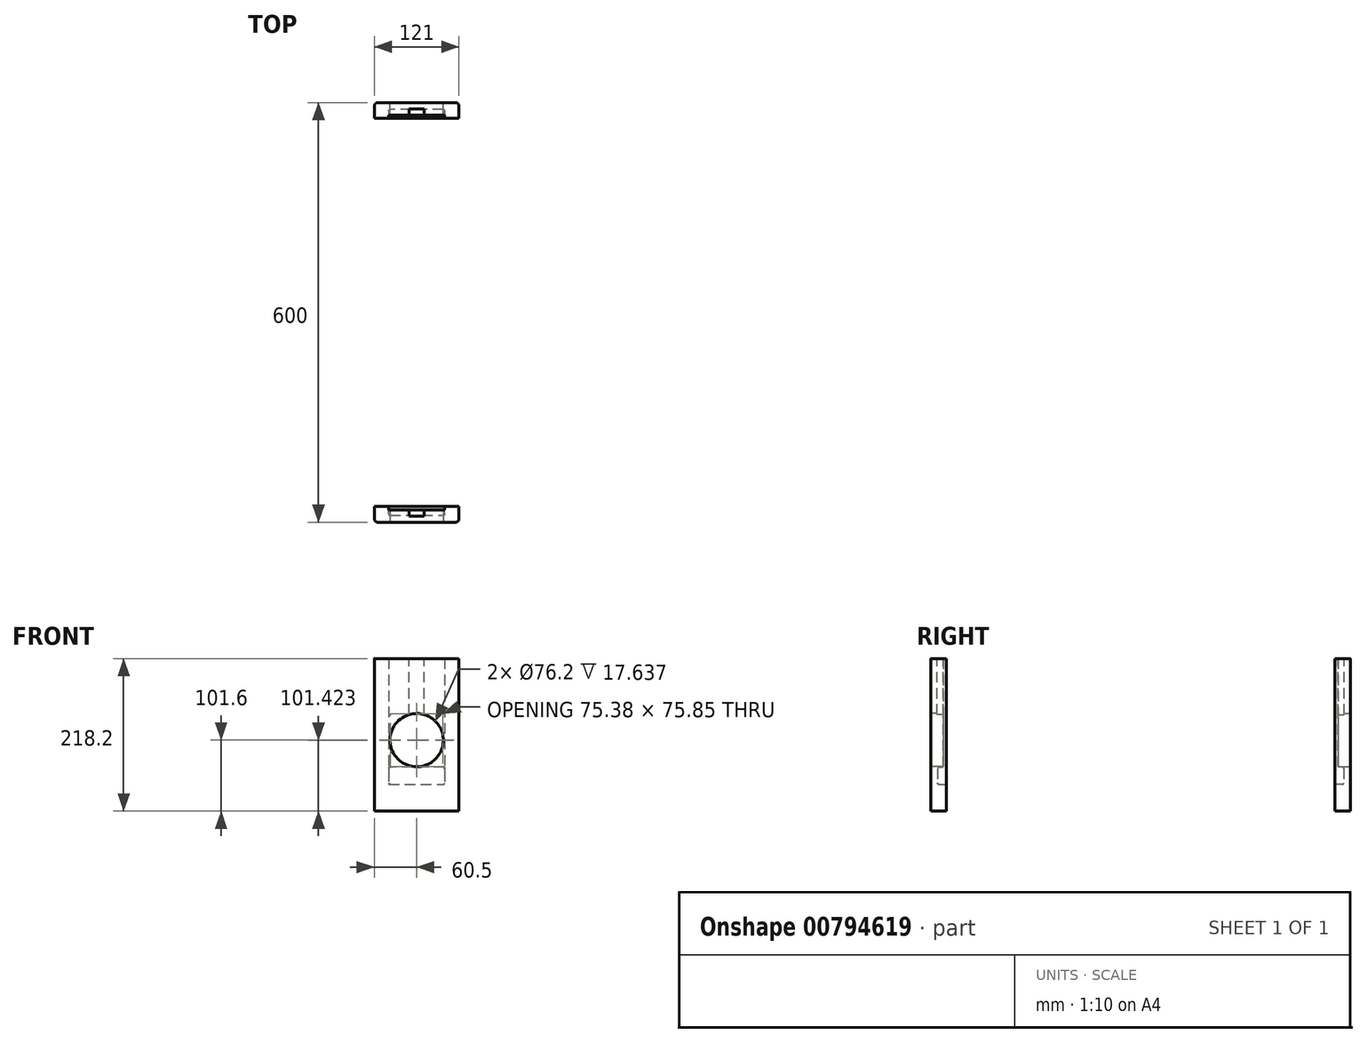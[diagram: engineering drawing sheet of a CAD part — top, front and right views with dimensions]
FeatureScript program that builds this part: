
annotation { "Feature Type Name" : "Feature", "Feature Type Description" : "" }
export const myFeature = defineFeature(function(context is Context, id is Id, definition is map)
    precondition{}
    {
        {
            var Q0;
            Q0=qCreatedBy(makeId("Front.planeOp"),FACE);
            var sketch = newSketch(context, id + "F0", { "sketchPlane" : qUnion([Q0])});
            skLineSegment(sketch, "E0.bottom", {"start": v(60.5, -109.1) * mm, "end": v(-60.5, -109.1) * mm});
            skLineSegment(sketch, "E0.top", {"start": v(60.5, 109.1) * mm, "end": v(-60.5, 109.1) * mm});
            skLineSegment(sketch, "E0.left", {"start": v(60.5, -109.1) * mm, "end": v(60.5, 109.1) * mm});
            skLineSegment(sketch, "E0.right", {"start": v(-60.5, -109.1) * mm, "end": v(-60.5, 109.1) * mm});
            skPoint(sketch, "E0.middle", {"position": v(0, 0) * mm});
            skCircle(sketch, "E1", {"center": v(0, -7.5) * mm, "radius": 38.1 * mm});
            skSolve(sketch);
        }
        {
            var Q0;
            Q0 = qSketchRegion(id + "F0", true);
            extrude(context, id + "F1", {"entities" : qUnion([Q0]), "depth" : 22.4 * mm, "offsetDistance" : 25 * mm});
        }
        {
            var Q0;
            Q0=makeQuery(id+"F1.opExtrude","CAP_FACE",FACE,{"disambiguationData":[OSD([sQuery(id+"F0.wireOp",EDGE,"E0.bottom"),sQuery(id+"F0.wireOp",EDGE,"E0.top"),sQuery(id+"F0.wireOp",EDGE,"E0.left"),sQuery(id+"F0.wireOp",EDGE,"E0.right"),sQuery(id+"F0.wireOp",EDGE,"E1")])],"isStart":false});
            var sketch = newSketch(context, id + "F2", { "sketchPlane" : qUnion([Q0])});
            skLineSegment(sketch, "E2.bottom", {"start": v(-40, 109.1) * mm, "end": v(40, 109.1) * mm});
            skLineSegment(sketch, "E2.top", {"start": v(-40, -71) * mm, "end": v(40, -71) * mm});
            skLineSegment(sketch, "E2.left", {"start": v(-40, 109.1) * mm, "end": v(-40, -71) * mm});
            skLineSegment(sketch, "E2.right", {"start": v(40, 109.1) * mm, "end": v(40, -71) * mm});
            skSolve(sketch);
        }
        {
            var Q0;
            Q0 = qSketchRegion(id + "F2", true);
            extrude(context, id + "F3", {"entities" : qUnion([Q0]), "operationType" : NewBodyOperationType.REMOVE, "oppositeDirection" : true, "depth" : 4.76 * mm, "offsetDistance" : 25 * mm});
        }
        {
            var Q0;
            Q0=makeQuery(id+"F1.opExtrude","CAP_FACE",FACE,{"disambiguationData":[OSD([sQuery(id+"F0.wireOp",EDGE,"E0.bottom"),sQuery(id+"F0.wireOp",EDGE,"E0.top"),sQuery(id+"F0.wireOp",EDGE,"E0.left"),sQuery(id+"F0.wireOp",EDGE,"E0.right"),sQuery(id+"F0.wireOp",EDGE,"E1")])],"isStart":false});
            var sketch = newSketch(context, id + "F4", { "sketchPlane" : qUnion([Q0])});
            skLineSegment(sketch, "E3.bottom", {"start": v(40, -71) * mm, "end": v(-40, -71) * mm});
            skLineSegment(sketch, "E3.top", {"start": v(40, -46) * mm, "end": v(-40, -46) * mm});
            skLineSegment(sketch, "E3.left", {"start": v(40, -71) * mm, "end": v(40, -46) * mm});
            skLineSegment(sketch, "E3.right", {"start": v(-40, -71) * mm, "end": v(-40, -46) * mm});
            skSolve(sketch);
        }
        {
            var Q0;
            Q0 = qSketchRegion(id + "F4", true);
            extrude(context, id + "F5", {"entities" : qUnion([Q0]), "operationType" : NewBodyOperationType.REMOVE, "oppositeDirection" : true, "depth" : 12.7 * mm, "offsetDistance" : 25 * mm});
        }
        {
            var Q0;
            Q0=makeQuery(id+"F1.opExtrude","CAP_EDGE",EDGE,{"disambiguationData":[OSD([sQuery(id+"F0.wireOp",EDGE,"E0.right")])],"isStart":true});
            var Q1;
            Q1=makeQuery(id+"F1.opExtrude","CAP_EDGE",EDGE,{"disambiguationData":[OSD([sQuery(id+"F0.wireOp",EDGE,"E0.left")])],"isStart":true});
            fillet(context, id + "F6", {"entities" : qUnion([Q0, Q1]), "radius" : 5 * mm, "tangentPropagation" : true, "allowEdgeOverflow" : false});
        }
        {
            var Q0;
            Q0=makeQuery(id+"F5.boolean.opBoolean","COPY",EDGE,{"derivedFrom":makeQuery(id+"F5.opExtrude","CAP_EDGE",EDGE,{"disambiguationData":[OSD([sQuery(id+"F4.wireOp",EDGE,"E3.bottom")])],"isStart":false})});
            var Q1;
            Q1=makeQuery(id+"F5.boolean.opBoolean","MERGE",EDGE,{"derivedFrom":[makeQuery(id+"F3.boolean.opBoolean","COPY",EDGE,{"derivedFrom":makeQuery(id+"F3.opExtrude","SWEPT_EDGE",EDGE,{"disambiguationData":[OSD([sQuery(id+"F2.wireOp",EDGE,"E2.top"),sQuery(id+"F2.wireOp",EDGE,"E2.right")])]})}),makeQuery(id+"F5.opExtrude","SWEPT_EDGE",EDGE,{"disambiguationData":[OSD([sQuery(id+"F4.wireOp",EDGE,"E3.bottom"),sQuery(id+"F4.wireOp",EDGE,"E3.left")])]})]});
            var Q2;
            Q2=makeQuery(id+"F5.boolean.opBoolean","COPY",EDGE,{"derivedFrom":makeQuery(id+"F5.opExtrude","CAP_EDGE",EDGE,{"disambiguationData":[OSD([sQuery(id+"F4.wireOp",EDGE,"E3.left")])],"isStart":false})});
            var Q3;
            Q3=makeQuery(id+"F5.boolean.opBoolean","COPY",EDGE,{"derivedFrom":makeQuery(id+"F5.opExtrude","CAP_EDGE",EDGE,{"disambiguationData":[OSD([sQuery(id+"F4.wireOp",EDGE,"E3.right")])],"isStart":false})});
            var Q4;
            Q4=makeQuery(id+"F5.boolean.opBoolean","COPY",EDGE,{"derivedFrom":makeQuery(id+"F5.opExtrude","CAP_EDGE",EDGE,{"disambiguationData":[OSD([sQuery(id+"F4.wireOp",EDGE,"E3.top")])],"isStart":false})});
            fillet(context, id + "F7", {"entities" : qUnion([Q0, Q1, Q2, Q3, Q4]), "radius" : 2 * mm, "tangentPropagation" : true, "allowEdgeOverflow" : false});
        }
        {
            var Q0;
            Q0=qCreatedBy(makeId("Front.planeOp"),FACE);
            cPlane(context, id + "F8", {"entities" : qUnion([Q0]), "cplaneType" : CPlaneType.OFFSET, "offset" : 300 * mm, "width" : 150 * mm, "height" : 150 * mm});
        }
        {
            var Q0;
            Q0=makeQuery(id+"F1.opExtrude","SWEPT_BODY",BODY,{"disambiguationData":[OSD([sQuery(id+"F0.wireOp",EDGE,"E0.bottom"),sQuery(id+"F0.wireOp",EDGE,"E0.top"),sQuery(id+"F0.wireOp",EDGE,"E0.left"),sQuery(id+"F0.wireOp",EDGE,"E0.right"),sQuery(id+"F0.wireOp",EDGE,"E1")])]});
            var Q1;
            Q1=qCreatedBy(id+"F8.planeOp",FACE);
            mirror(context, id + "F9", {"entities" : qUnion([Q0]), "mirrorPlane" : qUnion([Q1])});
        }
        {
            var Q0;
            Q0=makeQuery(id+"F1.opExtrude","SWEPT_FACE",FACE,{"disambiguationData":[OSD([sQuery(id+"F0.wireOp",EDGE,"E0.top")])]});
            var sketch = newSketch(context, id + "F10", { "sketchPlane" : qUnion([Q0])});
            skLineSegment(sketch, "E4", {"start": v(0, 0) * mm, "end": v(0, -17.64) * mm, "construction": true});
            skLineSegment(sketch, "E5", {"start": v(-11, -17.64) * mm, "end": v(-11, -8.86) * mm});
            skLineSegment(sketch, "E6", {"start": v(11, -17.64) * mm, "end": v(11, -8.86) * mm});
            skLineSegment(sketch, "E7", {"start": v(-11, -8.86) * mm, "end": v(11, -8.86) * mm});
            skLineSegment(sketch, "E8", {"start": v(-11, -17.64) * mm, "end": v(11, -17.64) * mm});
            skSolve(sketch);
        }
        {
            var Q0;
            Q0 = qSketchRegion(id + "F10", true);
            extrude(context, id + "F11", {"entities" : qUnion([Q0]), "operationType" : NewBodyOperationType.REMOVE, "oppositeDirection" : true, "depth" : 100 * mm, "offsetDistance" : 25 * mm});
        }
        {
            var Q0;
            Q0=makeQuery(id+"F9.opPattern","COPY",BODY,{"derivedFrom":makeQuery(id+"F1.opExtrude","SWEPT_BODY",BODY,{"disambiguationData":[OSD([sQuery(id+"F0.wireOp",EDGE,"E0.bottom"),sQuery(id+"F0.wireOp",EDGE,"E0.top"),sQuery(id+"F0.wireOp",EDGE,"E0.left"),sQuery(id+"F0.wireOp",EDGE,"E0.right"),sQuery(id+"F0.wireOp",EDGE,"E1")])]}),"instanceName":"1"});
            deleteBodies(context, id + "F12", {"entities" : qUnion([Q0])});
        }
        {
            var Q0;
            Q0=makeQuery(id+"F1.opExtrude","SWEPT_BODY",BODY,{"disambiguationData":[OSD([sQuery(id+"F0.wireOp",EDGE,"E0.bottom"),sQuery(id+"F0.wireOp",EDGE,"E0.top"),sQuery(id+"F0.wireOp",EDGE,"E0.left"),sQuery(id+"F0.wireOp",EDGE,"E0.right"),sQuery(id+"F0.wireOp",EDGE,"E1")])]});
            var Q1;
            Q1=qCreatedBy(id+"F8.planeOp",FACE);
            mirror(context, id + "F13", {"entities" : qUnion([Q0]), "mirrorPlane" : qUnion([Q1])});
        }
    });
